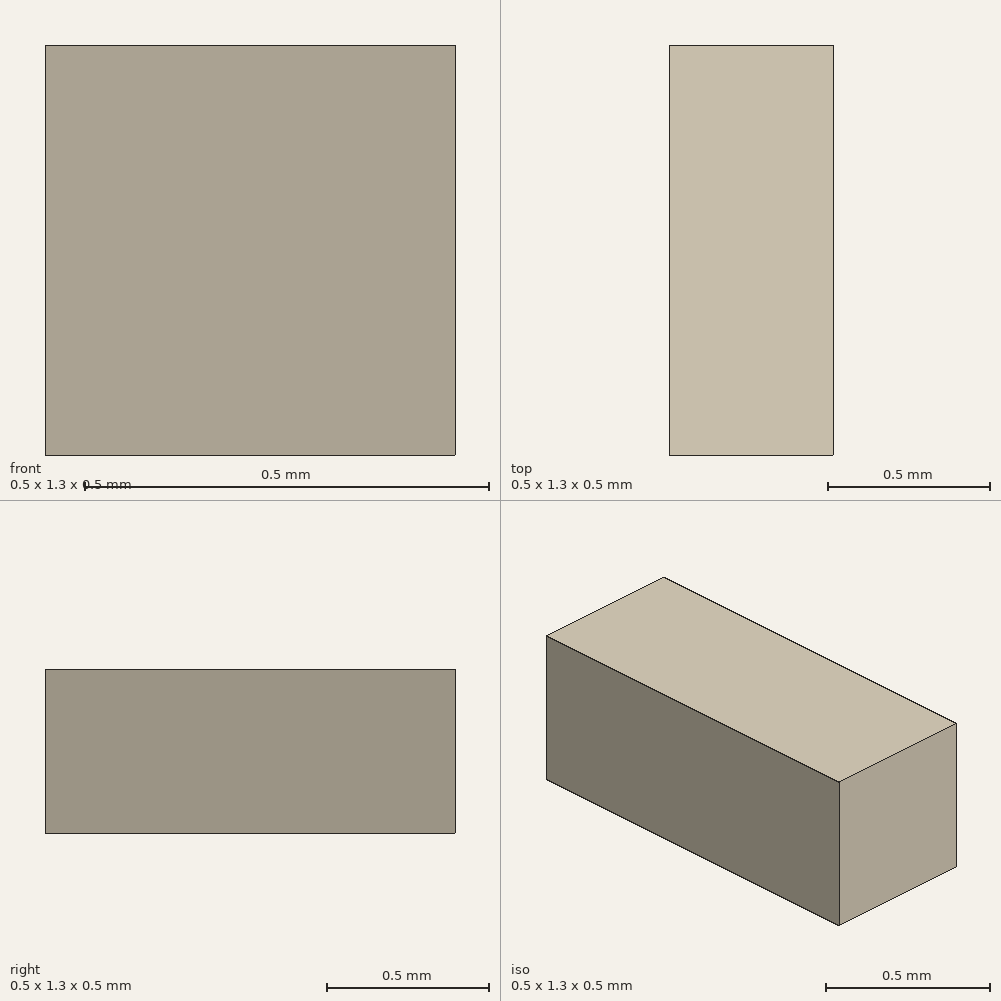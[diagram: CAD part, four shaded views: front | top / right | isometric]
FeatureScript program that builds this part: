
annotation { "Feature Type Name" : "Feature", "Feature Type Description" : "" }
export const myFeature = defineFeature(function(context is Context, id is Id, definition is map)
    precondition{}
    {
        {
            var Q0;
            Q0=qCreatedBy(makeId("Front.planeOp"),FACE);
            var sketch = newSketch(context, id + "F0", { "sketchPlane" : qUnion([Q0])});
            skLineSegment(sketch, "E0.bottom", {"start": v(-8.18, 11.6) * mm, "end": v(4.52, 11.6) * mm});
            skLineSegment(sketch, "E0.top", {"start": v(-8.18, 3.98) * mm, "end": v(4.52, 3.98) * mm});
            skLineSegment(sketch, "E0.left", {"start": v(-8.18, 11.6) * mm, "end": v(-8.18, 3.98) * mm});
            skLineSegment(sketch, "E0.right", {"start": v(4.52, 11.6) * mm, "end": v(4.52, 3.98) * mm});
            skLineSegment(sketch, "E1.bottom", {"start": v(-8.18, 8.05) * mm, "end": v(4.52, 8.05) * mm});
            skLineSegment(sketch, "E1.top", {"start": v(-8.18, 7.54) * mm, "end": v(4.52, 7.54) * mm});
            skLineSegment(sketch, "E1.left", {"start": v(-8.18, 8.05) * mm, "end": v(-8.18, 7.54) * mm});
            skLineSegment(sketch, "E1.right", {"start": v(4.52, 8.05) * mm, "end": v(4.52, 7.54) * mm});
            skLineSegment(sketch, "E2.bottom", {"start": v(-2.08, 11.6) * mm, "end": v(-1.58, 11.6) * mm});
            skLineSegment(sketch, "E2.top", {"start": v(-2.08, 3.98) * mm, "end": v(-1.58, 3.98) * mm});
            skLineSegment(sketch, "E2.left", {"start": v(-2.08, 11.6) * mm, "end": v(-2.08, 3.98) * mm});
            skLineSegment(sketch, "E2.right", {"start": v(-1.58, 11.6) * mm, "end": v(-1.58, 3.98) * mm});
            skLineSegment(sketch, "E3.bottom", {"start": v(-8.43, 11.86) * mm, "end": v(4.77, 11.86) * mm});
            skLineSegment(sketch, "E3.top", {"start": v(-8.43, 3.73) * mm, "end": v(4.77, 3.73) * mm});
            skLineSegment(sketch, "E3.left", {"start": v(-8.43, 11.86) * mm, "end": v(-8.43, 3.73) * mm});
            skLineSegment(sketch, "E3.right", {"start": v(4.77, 11.86) * mm, "end": v(4.77, 3.73) * mm});
            skSolve(sketch);
        }
        {
            var Q0;
            {var subQ10=sQuery(id+"F0.wireOp",EDGE,"E1.left");Q0=makeQuery(id+"F0.imprint","IMPRINT",FACE,{"disambiguationData":[TD([[makeQuery(id+"F0.imprint","IMPRINT",EDGE,{"derivedFrom":subQ10}),-1.0]])]});}
            var Q1;
            {var subQ0=sQuery(id+"F0.wireOp",EDGE,"E1.left");Q1=makeQuery(id+"F0.imprint","IMPRINT",FACE,{"disambiguationData":[TD([[makeQuery(id+"F0.imprint","IMPRINT",EDGE,{"derivedFrom":subQ0}),1.0]])]});}
            var Q2;
            {var subQ0=sQuery(id+"F0.wireOp",EDGE,"E1.right");Q2=makeQuery(id+"F0.imprint","IMPRINT",FACE,{"disambiguationData":[TD([[makeQuery(id+"F0.imprint","IMPRINT",EDGE,{"derivedFrom":subQ0}),-1.0]])]});}
            var Q3;
            {var subQ0=sQuery(id+"F0.wireOp",EDGE,"E2.left");var subQ1=sQuery(id+"F0.wireOp",EDGE,"E1.bottom");var subQ2=makeQuery(id+"F0.imprint","INTERSECT",VERTEX,{"derivedFrom":[subQ1,subQ0]});Q3=makeQuery(id+"F0.imprint","IMPRINT",FACE,{"disambiguationData":[TD([[makeQuery(id+"F0.imprint","IMPRINT",EDGE,{"disambiguationData":[TD([[subQ2,-1.0]])],"derivedFrom":subQ1}),-1.0]])]});}
            var Q4;
            {var subQ5=sQuery(id+"F0.wireOp",EDGE,"E2.bottom");Q4=makeQuery(id+"F0.imprint","IMPRINT",FACE,{"disambiguationData":[TD([[makeQuery(id+"F0.imprint","IMPRINT",EDGE,{"derivedFrom":subQ5}),-1.0]])]});}
            var Q5;
            {var subQ5=sQuery(id+"F0.wireOp",EDGE,"E2.top");Q5=makeQuery(id+"F0.imprint","IMPRINT",FACE,{"disambiguationData":[TD([[makeQuery(id+"F0.imprint","IMPRINT",EDGE,{"derivedFrom":subQ5}),1.0]])]});}
            extrude(context, id + "F1", {"entities" : qUnion([Q0, Q1, Q2, Q3, Q4, Q5]), "endBound" : BoundingType.SYMMETRIC, "depth" : 1.27 * mm, "offsetDistance" : 25.4 * mm});
        }
    });
